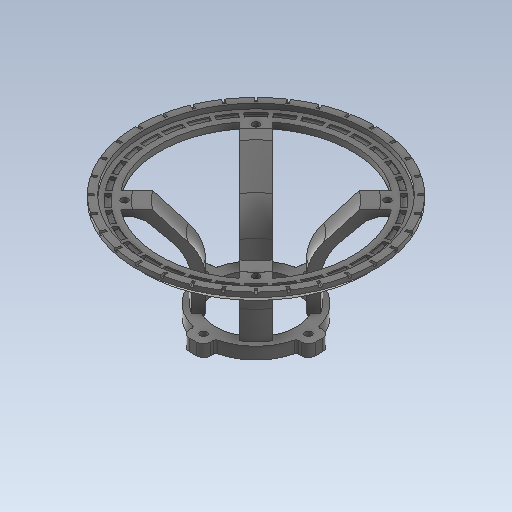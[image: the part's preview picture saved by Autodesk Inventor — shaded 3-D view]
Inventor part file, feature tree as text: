
AUTODESK INVENTOR PART (.ipt)
format: ipt  version: 2020 (Build 240168000, 168)  size: 1,808,384 bytes
history: native  units: mm
features: projected_geometry x28, other x27, sketch x23, extrude x13, fillet x10, revolve x9, pattern_circular x6, loft x6, mirror x5, chamfer x2
ambient origin geometry x8: Origin, YZ Plane, XZ Plane, XY Plane, X Axis, Y Axis, Z Axis, Center Point
bodies: Body1 (feature_tree)
feature tree (129):
  other  "Твердое тело1"
  extrude  "Выдавливание1"  Depth=34.0mm
  other  "РабПлоскость1"
  other  "РабОсь1"
  revolve  "Вращение1"
  extrude  "Выдавливание2"  Depth=45.0mm
  other  "РабТочка2"
  other  "РабТочка3"
  other  "РабТочка4"
  other  "РабПлоскость2"
  sketch  "Эскиз5"
  revolve  "Вращение2"
  revolve  "Вращение3"
  pattern_circular  "Круговой массив1"  Angle=45.0deg  [1 undecoded]
  extrude  "Выдавливание3"  Depth=2.9mm
  revolve  "Вращение4"
  fillet  "Сопряжение1"  Radius=9.0mm
  revolve  "Вращение5"
  other  "РабПлоскость6"
  other  "РабПлоскость7"
  sketch  "Эскиз10"
  revolve  "Вращение6"
  revolve  "Вращение7"
  sketch  "Эскиз11"
  sketch  "Эскиз12"
  loft  "Лофт2"
  loft  "Лофт3"
  fillet  "Сопряжение2"  Radius=1.0mm
  extrude  "Выдавливание4"  Depth=22.0mm
  loft  "Лофт4"
  fillet  "Сопряжение3"  Radius=5.0mm
  pattern_circular  "Круговой массив2"  [2 undecoded]
  revolve  "Вращение8"
  revolve  "Вращение9"
  extrude  "Выдавливание5"  Depth=2.5mm
  extrude  "Выдавливание6"  Depth=45.0mm
  pattern_circular  "Круговой массив3"  [2 undecoded]
  other  "РабПлоскость8"
  extrude  "Выдавливание8"  Depth=2.0mm
  extrude  "Выдавливание7"  Depth=2.0mm
  loft  "Лофт5"
  pattern_circular  "Круговой массив4"  Angle=45.0deg  [1 undecoded]
  fillet  "Сопряжение4"  [1 undecoded]
  chamfer  "Фаска1"  Distance=3.0mm
  sketch  "Эскиз23"
  extrude  "Выдавливание9"  TaperAngle=135.0deg  [1 undecoded]
  loft  "Лофт6"
  other  "РабПлоскость9"
  mirror  "Зеркальное отражение1"
  pattern_circular  "Круговой массив5"  [2 undecoded]
  extrude  "Выдавливание10"  TaperAngle=0.0deg  [1 undecoded]
  pattern_circular  "Круговой массив6"  [2 undecoded]
  other  "board plane"
  sketch  "Эскиз26"
  extrude  "Выдавливание11"  Depth=10.0mm
  extrude  "Выдавливание12"  Depth=2.0mm
  other  "РабПлоскость11"
  sketch  "Эскиз28"
  other  "РабПлоскость12"
  loft  "Лофт9"
  fillet  "Сопряжение5"  [1 undecoded]
  other  "РабПлоскость13"
  extrude  "Выдавливание13"  Depth=2.5mm
  chamfer  "Фаска2"  Angle=90.0deg  [1 undecoded]
  other  "РабПлоскость14"
  mirror  "Зеркальное отражение4"
  mirror  "Зеркальное отражение5"
  fillet  "Сопряжение6"  [1 undecoded]
  other  "РабПлоскость15"
  mirror  "Зеркальное отражение6"
  mirror  "Зеркальное отражение7"
  fillet  "Сопряжение8"  Radius=40.0mm
  fillet  "Сопряжение9"  Radius=78.0mm
  fillet  "Сопряжение10"  [1 undecoded]
  fillet  "Сопряжение11"  Radius=2.9mm
  sketch  "Эскиз1"
  sketch  "Эскиз2"
  sketch  "Эскиз4"
  projected_geometry  "Спроецированная петля1"
  projected_geometry  "Спроецированная петля2"
  projected_geometry  "Спроецированная петля3"
  other  "РабПлоскость3"
  other  "РабПлоскость4"
  other  "РабПлоскость5"
  sketch  "Эскиз6"
  sketch  "Эскиз7"
  sketch  "Эскиз9"
  projected_geometry  "Спроецированная петля4"
  projected_geometry  "Спроецированная петля5"
  other  "Ребра2"
  other  "Ребра3"
  sketch  "Эскиз13"
  projected_geometry  "Спроецированная петля6"
  projected_geometry  "Спроецированная петля7"
  sketch  "Эскиз14"
  projected_geometry  "Спроецированная петля8"
  projected_geometry  "Спроецированная петля9"
  projected_geometry  "Спроецированная петля10"
  sketch  "Эскиз16"
  sketch  "Эскиз17"
  projected_geometry  "Спроецированная петля12"
  projected_geometry  "Спроецированная петля13"
  sketch  "Эскиз18"
  sketch  "Эскиз19"
  projected_geometry  "Спроецированная петля14"
  projected_geometry  "Спроецированная петля15"
  other  "Ребра5"
  sketch  "Эскиз22"
  projected_geometry  "Спроецированная петля16"
  projected_geometry  "Спроецированная петля17"
  projected_geometry  "Спроецированная петля18"
  projected_geometry  "Спроецированная петля19"
  projected_geometry  "Спроецированная петля20"
  sketch  "Эскиз24"
  other  "Ребра6"
  sketch  "Эскиз25"
  projected_geometry  "Спроецированная петля21"
  projected_geometry  "Спроецированная петля22"
  projected_geometry  "Спроецированная петля23"
  projected_geometry  "Спроецированная петля24"
  projected_geometry  "Спроецированная петля27"
  projected_geometry  "Спроецированная петля28"
  projected_geometry  "Спроецированная петля29"
  projected_geometry  "Спроецированная петля30"
  sketch  "Эскиз29"
  other  "Ребра15"
  projected_geometry  "Спроецированная петля31"
  other  "Ребра16"
  other  "Ребра17"
note: 17 required parameter values undecoded (feature->parameter linkage not recoverable at this tier; creation-order binding heuristic only, values carry confidence <= 0.55)
